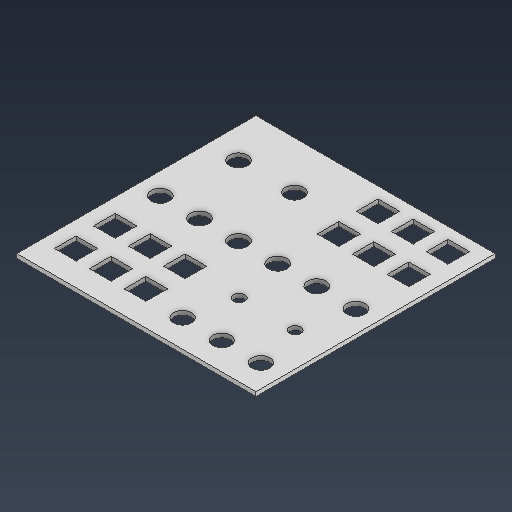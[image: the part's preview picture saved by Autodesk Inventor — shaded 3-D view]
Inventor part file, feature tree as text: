
AUTODESK INVENTOR PART (.ipt)
format: ipt  version: 2025.3 (Build 293356000, 356)  size: 580,096 bytes
history: native  units: mm
features: projected_geometry x26, sketch x20, extrude x8, fillet x1
ambient origin geometry x8: Origin, YZ Plane, XZ Plane, XY Plane, X Axis, Y Axis, Z Axis, Center Point
bodies: Solid1 (feature_tree)
feature tree (55):
  extrude  "Extrusion1"  Depth=171.0mm
  extrude  "Extrusion3"  Depth=60.0mm
  extrude  "Extrusion5"  Depth=78.0mm
  extrude  "Extrusion6"  Depth=75.0mm
  extrude  "Extrusion7"  Depth=30.0mm
  extrude  "Extrusion8"  Depth=5.0mm
  extrude  "Extrusion9"  Depth=25.0mm
  fillet  "Fillet1"  Radius=25.0mm
  extrude  "Extrusion10"  Depth=15.4mm
  sketch  "Sketch1"  dims[d0=171.0mm d1=171.0mm]
  sketch  "Sketch3"  dims[d10=78.0mm d11=78.0mm]
  sketch  "Sketch Rectangular Pattern1"  dims[d2=3.0mm d3=0.0mm d9=60.0mm]
  sketch  "Sketch Rectangular Pattern4"  dims[d12=60.0mm d17=75.0mm]
  sketch  "Sketch5"  dims[d20=5.0mm d21=30.0mm]
  sketch  "Sketch7"  dims[d32=15.4mm d33=15.4mm]
  projected_geometry  "Projected Loop3"
  sketch  "Sketch Rectangular Pattern5"  dims[d22=5.0mm d23=5.0mm]
  sketch  "Sketch8"  dims[d43=12.6mm]
  projected_geometry  "Projected Loop4"
  sketch  "Sketch Rectangular Pattern6"  dims[d27=5.0mm d28=5.0mm d31=25.0mm]
  sketch  "Sketch Rectangular Pattern7"  dims[d35=20.0mm d37=28.0mm d38=30.0mm d40=25.0mm]
  sketch  "Sketch Rectangular Pattern9"  dims[d44=6.3mm]
  sketch  "Sketch9"  dims[d45=4.0mm]
  projected_geometry  "Projected Loop5"
  projected_geometry  "Projected Loop6"
  projected_geometry  "Projected Loop7"
  projected_geometry  "Projected Loop8"
  projected_geometry  "Projected Loop9"
  projected_geometry  "Projected Loop10"
  projected_geometry  "Projected Loop11"
  projected_geometry  "Projected Loop12"
  sketch  "Sketch Rectangular Pattern11"  dims[d47=11.7mm]
  sketch  "Sketch Rectangular Pattern15"  dims[d52=15.4mm d53=15.4mm d54=28.0mm d55=25.0mm]
  projected_geometry  "Projected Loop26"
  projected_geometry  "Projected Loop27"
  projected_geometry  "Projected Loop28"
  projected_geometry  "Projected Loop29"
  projected_geometry  "Projected Loop30"
  projected_geometry  "Projected Loop31"
  projected_geometry  "Projected Loop32"
  projected_geometry  "Projected Loop33"
  projected_geometry  "Projected Loop34"
  projected_geometry  "Projected Loop35"
  projected_geometry  "Projected Loop36"
  projected_geometry  "Projected Loop37"
  projected_geometry  "Projected Loop38"
  projected_geometry  "Projected Loop39"
  projected_geometry  "Projected Loop40"
  projected_geometry  "Projected Loop41"
  sketch  "Sketch Rectangular Pattern16"  dims[d56=12.6mm]
  sketch  "Sketch Rectangular Pattern17"  dims[d57=30.0mm]
  sketch  "Sketch Rectangular Pattern18"  dims[d58=80.0mm]
  sketch  "Sketch Rectangular Pattern19"  dims[d59=25.0mm d60=25.0mm d61=20.0mm d62=40.0mm d63=8.0mm d64=8.0mm d65=10.0mm d66=0.0mm d67=80.0mm d68=16.2mm d69=16.2mm d70=16.2mm d71=28.0mm d72=28.0mm d73=12.0mm d74=12.8mm d75=12.8mm d76=12.8mm d77=13.0mm d78=60.0mm d80=28.0mm d81=10.0mm d83=10.0mm d85=11.5mm d86=163.0mm d87=65.0mm d88=95.0mm d89=88.0mm d90=13.0mm d91=13.0mm d92=30.0mm d93=40.0mm d94=17.5mm d99=13.0mm d100=28.8mm d101=17.2mm d102=17.2mm d103=1.0mm d104=0.0mm d105=4.0mm d106=4.0mm d107=4.0mm d108=4.0mm d109=4.0mm d110=4.0mm d111=7.0mm d112=4.0mm d113=4.0mm d114=4.0mm d115=4.5mm d116=5.0mm d117=22.0mm d118=12.0mm d119=6.0mm d120=10.0mm d121=0.0mm d122=3.0mm d123=60.0mm d125=28.0mm d126=10.0mm d128=10.0mm d130=3.0mm d131=3.0mm d132=3.0mm d133=3.0mm d134=3.0mm d135=10.0mm d136=6.0mm d137=80.0mm d139=20.0mm d140=10.0mm d142=10.0mm d145=10.0mm d146=40.0mm d148=20.0mm d149=10.0mm d151=10.0mm d153=16.0mm d154=10.0mm d162=10.0mm d163=16.0mm d164=5.0mm d165=0.0mm d166=30.0mm d168=20.0mm d169=10.0mm d171=10.0mm d181=10.0mm d182=80.0mm d184=20.0mm d185=10.0mm d187=10.0mm d215=10.0mm d216=0.0mm d217=6.0mm d218=70.0mm d220=20.0mm d221=10.0mm d223=10.0mm d225=10.0mm d226=10.0mm d227=10.0mm d228=10.0mm d229=10.0mm d230=10.0mm d231=10.0mm d232=10.0mm d233=30.0mm d235=20.0mm d236=10.0mm d238=10.0mm d240=40.0mm d242=20.0mm d243=10.0mm d245=10.0mm d247=30.0mm d249=20.0mm d250=10.0mm d252=10.0mm d254=30.0mm d256=20.0mm d257=10.0mm d259=10.0mm d261=2.7mm d262=10.0mm d263=0.0mm d264=1.0mm d265=3.0mm d266=2.0mm d267=0.0mm]
  sketch  "Sketch10"  dims[d46=14.0mm]
  sketch  "Sketch11"  dims[d49=20.0mm d51=30.0mm]
